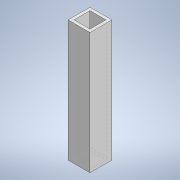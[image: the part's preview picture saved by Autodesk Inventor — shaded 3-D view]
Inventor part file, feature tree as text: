
AUTODESK INVENTOR PART (.ipt)
format: ipt  version: 2020.3 (Build 243373000, 373)  size: 140,288 bytes
history: native  units: mm
features: sketch x5, hole x4, other x1, extrude x1
ambient origin geometry x8: Origin, YZ Plane, XZ Plane, XY Plane, X Axis, Y Axis, Z Axis, Center Point
bodies: Body1 (feature_tree)
feature tree (11):
  other  "ソリッド1"
  extrude  "押し出し1"  Depth=9.0mm
  hole  "穴1"  [1 undecoded]
  hole  "穴2"  [1 undecoded]
  hole  "穴3"  [1 undecoded]
  hole  "穴4"  [1 undecoded]
  sketch  "スケッチ1"
  sketch  "スケッチ2"
  sketch  "スケッチ3"
  sketch  "スケッチ4"
  sketch  "スケッチ5"
note: 4 required parameter values undecoded (feature->parameter linkage not recoverable at this tier; creation-order binding heuristic only, values carry confidence <= 0.55)
